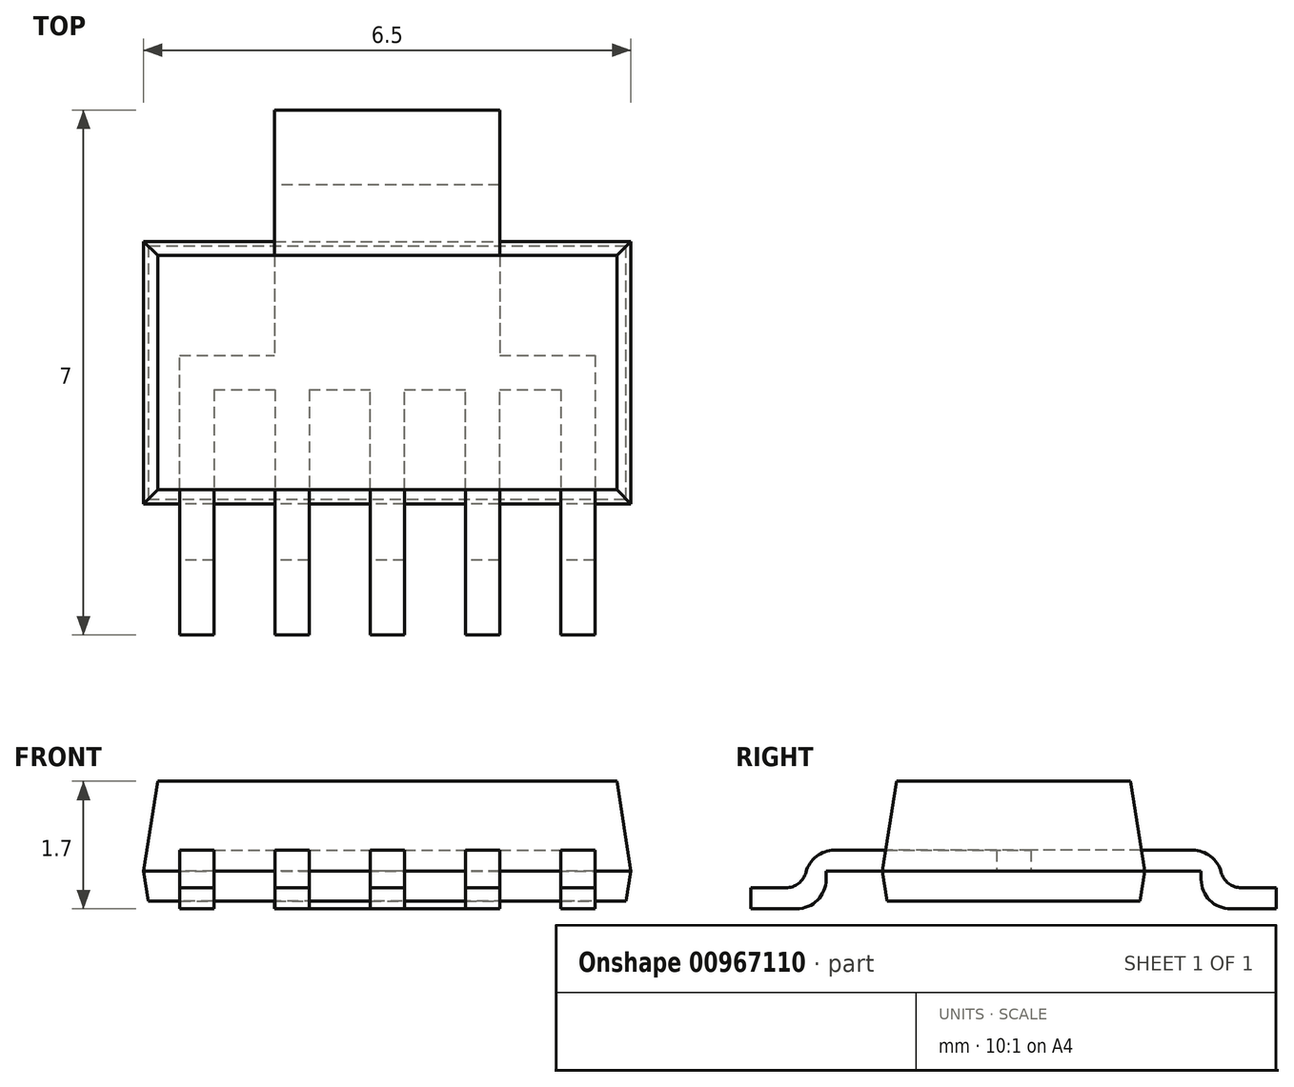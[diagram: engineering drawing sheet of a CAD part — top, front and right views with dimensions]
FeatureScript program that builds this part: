
annotation { "Feature Type Name" : "Feature", "Feature Type Description" : "" }
export const myFeature = defineFeature(function(context is Context, id is Id, definition is map)
    precondition{}
    {
        {
            assignVariable(context, id + "F0", {"name" : "A2", "anyValue" : 1.6});
        }
        {
            assignVariable(context, id + "F1", {"name" : "A1", "anyValue" : 0.1});
        }
        {
            assignVariable(context, id + "F2", {"name" : "c", "anyValue" : 0.28});
        }
        {
            var Q0;
            Q0=qCreatedBy(makeId("Top.planeOp"),FACE);
            var sketch = newSketch(context, id + "F3", { "sketchPlane" : qUnion([Q0])});
            skLineSegment(sketch, "E0.bottom", {"start": v(3.25, -1.75) * mm, "end": v(-3.25, -1.75) * mm});
            skLineSegment(sketch, "E0.top", {"start": v(3.25, 1.75) * mm, "end": v(-3.25, 1.75) * mm});
            skLineSegment(sketch, "E0.left", {"start": v(3.25, -1.75) * mm, "end": v(3.25, 1.75) * mm});
            skLineSegment(sketch, "E0.right", {"start": v(-3.25, -1.75) * mm, "end": v(-3.25, 1.75) * mm});
            skPoint(sketch, "E0.middle", {"position": v(0, 0) * mm});
            skLineSegment(sketch, "E1.bottom", {"start": v(-2.31, 0) * mm, "end": v(-2.77, 0) * mm});
            skLineSegment(sketch, "E1.top", {"start": v(-2.31, -3.5) * mm, "end": v(-2.77, -3.5) * mm});
            skLineSegment(sketch, "E1.left", {"start": v(-2.31, 0) * mm, "end": v(-2.31, -3.5) * mm});
            skLineSegment(sketch, "E1.right", {"start": v(-2.77, 0) * mm, "end": v(-2.77, -3.5) * mm});
            skPoint(sketch, "E1.middle", {"position": v(-2.54, -1.75) * mm});
            skLineSegment(sketch, "E2.bottom", {"start": v(0.23, -3.5) * mm, "end": v(-0.23, -3.5) * mm});
            skLineSegment(sketch, "E2.top", {"start": v(0.23, 0) * mm, "end": v(-0.23, 0) * mm});
            skLineSegment(sketch, "E2.left", {"start": v(0.23, -3.5) * mm, "end": v(0.23, 0) * mm});
            skLineSegment(sketch, "E2.right", {"start": v(-0.23, -3.5) * mm, "end": v(-0.23, 0) * mm});
            skPoint(sketch, "E2.middle", {"position": v(0, -1.75) * mm});
            skLineSegment(sketch, "E3.bottom", {"start": v(2.31, 0) * mm, "end": v(2.77, 0) * mm});
            skLineSegment(sketch, "E3.top", {"start": v(2.31, -3.5) * mm, "end": v(2.77, -3.5) * mm});
            skLineSegment(sketch, "E3.left", {"start": v(2.31, 0) * mm, "end": v(2.31, -3.5) * mm});
            skLineSegment(sketch, "E3.right", {"start": v(2.77, 0) * mm, "end": v(2.77, -3.5) * mm});
            skPoint(sketch, "E3.middle", {"position": v(2.54, -1.75) * mm});
            skLineSegment(sketch, "E4.bottom", {"start": v(1.5, 3.5) * mm, "end": v(-1.5, 3.5) * mm});
            skLineSegment(sketch, "E4.top", {"start": v(1.5, 0) * mm, "end": v(-1.5, 0) * mm});
            skLineSegment(sketch, "E4.left", {"start": v(1.5, 3.5) * mm, "end": v(1.5, 0) * mm});
            skLineSegment(sketch, "E4.right", {"start": v(-1.5, 3.5) * mm, "end": v(-1.5, 0) * mm});
            skPoint(sketch, "E4.middle", {"position": v(0, 1.75) * mm});
            skLineSegment(sketch, "E5", {"start": v(0, 0) * mm, "end": v(0, 1.75) * mm, "construction": true});
            skLineSegment(sketch, "E6", {"start": v(0, 0) * mm, "end": v(0, -1.75) * mm, "construction": true});
            skLineSegment(sketch, "E7.bottom", {"start": v(-2.77, -0.23) * mm, "end": v(2.77, -0.23) * mm});
            skLineSegment(sketch, "E7.top", {"start": v(-2.77, 0.23) * mm, "end": v(2.77, 0.23) * mm});
            skLineSegment(sketch, "E7.left", {"start": v(-2.77, -0.23) * mm, "end": v(-2.77, 0.23) * mm});
            skLineSegment(sketch, "E7.right", {"start": v(2.77, -0.23) * mm, "end": v(2.77, 0.23) * mm});
            skLineSegment(sketch, "E8", {"start": v(-2.77, -2.78) * mm, "end": v(2.77, -2.78) * mm});
            skLineSegment(sketch, "E9", {"start": v(2.77, -2.5) * mm, "end": v(-2.77, -2.5) * mm});
            skLineSegment(sketch, "E10", {"start": v(-1.5, 2.78) * mm, "end": v(1.5, 2.78) * mm});
            skLineSegment(sketch, "E11", {"start": v(1.5, 2.5) * mm, "end": v(-1.5, 2.5) * mm});
            skLineSegment(sketch, "E12.bottom", {"start": v(-1.04, 0) * mm, "end": v(-1.5, 0) * mm});
            skLineSegment(sketch, "E12.top", {"start": v(-1.04, -3.5) * mm, "end": v(-1.5, -3.5) * mm});
            skLineSegment(sketch, "E12.left", {"start": v(-1.04, 0) * mm, "end": v(-1.04, -3.5) * mm});
            skLineSegment(sketch, "E12.right", {"start": v(-1.5, 0) * mm, "end": v(-1.5, -3.5) * mm});
            skPoint(sketch, "E12.middle", {"position": v(-1.27, -1.75) * mm});
            skLineSegment(sketch, "E13.bottom", {"start": v(1.04, -3.5) * mm, "end": v(1.5, -3.5) * mm});
            skLineSegment(sketch, "E13.top", {"start": v(1.04, 0) * mm, "end": v(1.5, 0) * mm});
            skLineSegment(sketch, "E13.left", {"start": v(1.04, -3.5) * mm, "end": v(1.04, 0) * mm});
            skLineSegment(sketch, "E13.right", {"start": v(1.5, -3.5) * mm, "end": v(1.5, 0) * mm});
            skPoint(sketch, "E13.middle", {"position": v(1.27, -1.75) * mm});
            skLineSegment(sketch, "E14", {"start": v(1.5, -2.78) * mm, "end": v(2.77, -2.78) * mm});
            skLineSegment(sketch, "E15", {"start": v(1.5, -2.5) * mm, "end": v(2.77, -2.5) * mm});
            skLineSegment(sketch, "E16", {"start": v(-1.5, -2.5) * mm, "end": v(-2.77, -2.5) * mm});
            skLineSegment(sketch, "E17", {"start": v(-1.5, -2.78) * mm, "end": v(-2.77, -2.78) * mm});
            skLineSegment(sketch, "E18", {"start": v(0, -1.75) * mm, "end": v(-1.27, -1.75) * mm, "construction": true});
            skLineSegment(sketch, "E19", {"start": v(-1.27, -1.75) * mm, "end": v(-2.54, -1.75) * mm, "construction": true});
            skLineSegment(sketch, "E20", {"start": v(0, -1.75) * mm, "end": v(1.27, -1.75) * mm, "construction": true});
            skLineSegment(sketch, "E21", {"start": v(1.27, -1.75) * mm, "end": v(2.54, -1.75) * mm, "construction": true});
            skSolve(sketch);
        }
        {
            var Q0;
            {var subQ4=sQuery(id+"F3.wireOp",EDGE,"E0.left");Q0=makeQuery(id+"F3.imprint","IMPRINT",FACE,{"disambiguationData":[TD([[makeQuery(id+"F3.imprint","IMPRINT",EDGE,{"derivedFrom":subQ4}),1.0]])]});}
            var Q1;
            {var subQ0=sQuery(id+"F3.wireOp",EDGE,"E4.left");var subQ1=sQuery(id+"F3.wireOp",EDGE,"E0.top");var subQ2=makeQuery(id+"F3.imprint","INTERSECT",VERTEX,{"derivedFrom":[subQ1,subQ0]});Q1=makeQuery(id+"F3.imprint","IMPRINT",FACE,{"disambiguationData":[TD([[makeQuery(id+"F3.imprint","IMPRINT",EDGE,{"disambiguationData":[TD([[subQ2,-1.0]])],"derivedFrom":subQ1}),1.0]])]});}
            var Q2;
            {var subQ0=sQuery(id+"F3.wireOp",EDGE,"E3.left");var subQ1=sQuery(id+"F3.wireOp",EDGE,"E0.bottom");var subQ2=makeQuery(id+"F3.imprint","INTERSECT",VERTEX,{"derivedFrom":[subQ1,subQ0]});Q2=makeQuery(id+"F3.imprint","IMPRINT",FACE,{"disambiguationData":[TD([[makeQuery(id+"F3.imprint","IMPRINT",EDGE,{"disambiguationData":[TD([[subQ2,-1.0]])],"derivedFrom":subQ1}),-1.0]])]});}
            var Q3;
            {var subQ3=sQuery(id+"F3.wireOp",EDGE,"E2.top");Q3=makeQuery(id+"F3.imprint","IMPRINT",FACE,{"disambiguationData":[TD([[makeQuery(id+"F3.imprint","IMPRINT",EDGE,{"derivedFrom":subQ3}),-1.0]])]});}
            var Q4;
            {var subQ0=sQuery(id+"F3.wireOp",EDGE,"E3.left");var subQ1=sQuery(id+"F3.wireOp",EDGE,"E0.bottom");var subQ2=makeQuery(id+"F3.imprint","INTERSECT",VERTEX,{"derivedFrom":[subQ1,subQ0]});Q4=makeQuery(id+"F3.imprint","IMPRINT",FACE,{"disambiguationData":[TD([[makeQuery(id+"F3.imprint","IMPRINT",EDGE,{"disambiguationData":[TD([[subQ2,1.0]])],"derivedFrom":subQ1}),-1.0]])]});}
            var Q5;
            {var subQ0=sQuery(id+"F3.wireOp",EDGE,"E2.right");var subQ1=sQuery(id+"F3.wireOp",EDGE,"E0.bottom");var subQ2=makeQuery(id+"F3.imprint","INTERSECT",VERTEX,{"derivedFrom":[subQ1,subQ0]});Q5=makeQuery(id+"F3.imprint","IMPRINT",FACE,{"disambiguationData":[TD([[makeQuery(id+"F3.imprint","IMPRINT",EDGE,{"disambiguationData":[TD([[subQ2,1.0]])],"derivedFrom":subQ1}),-1.0]])]});}
            var Q6;
            {var subQ0=sQuery(id+"F3.wireOp",EDGE,"E2.top");Q6=makeQuery(id+"F3.imprint","IMPRINT",FACE,{"disambiguationData":[TD([[makeQuery(id+"F3.imprint","IMPRINT",EDGE,{"derivedFrom":subQ0}),1.0]])]});}
            var Q7;
            {var subQ0=sQuery(id+"F3.wireOp",EDGE,"E2.right");var subQ1=sQuery(id+"F3.wireOp",EDGE,"E0.bottom");var subQ2=makeQuery(id+"F3.imprint","INTERSECT",VERTEX,{"derivedFrom":[subQ1,subQ0]});Q7=makeQuery(id+"F3.imprint","IMPRINT",FACE,{"disambiguationData":[TD([[makeQuery(id+"F3.imprint","IMPRINT",EDGE,{"disambiguationData":[TD([[subQ2,-1.0]])],"derivedFrom":subQ1}),-1.0]])]});}
            var Q8;
            {var subQ4=sQuery(id+"F3.wireOp",EDGE,"E0.right");Q8=makeQuery(id+"F3.imprint","IMPRINT",FACE,{"disambiguationData":[TD([[makeQuery(id+"F3.imprint","IMPRINT",EDGE,{"derivedFrom":subQ4}),-1.0]])]});}
            var Q9;
            {var subQ0=sQuery(id+"F3.wireOp",EDGE,"E1.right");var subQ1=sQuery(id+"F3.wireOp",EDGE,"E0.bottom");var subQ2=makeQuery(id+"F3.imprint","INTERSECT",VERTEX,{"derivedFrom":[subQ1,subQ0]});Q9=makeQuery(id+"F3.imprint","IMPRINT",FACE,{"disambiguationData":[TD([[makeQuery(id+"F3.imprint","IMPRINT",EDGE,{"disambiguationData":[TD([[subQ2,1.0]])],"derivedFrom":subQ1}),-1.0]])]});}
            var Q10;
            {var subQ1=sQuery(id+"F3.wireOp",EDGE,"E2.left");var subQ3=sQuery(id+"F3.wireOp",EDGE,"E7.bottom");var subQ4=makeQuery(id+"F3.imprint","INTERSECT",VERTEX,{"derivedFrom":[subQ1,subQ3]});Q10=makeQuery(id+"F3.imprint","IMPRINT",FACE,{"disambiguationData":[TD([[makeQuery(id+"F3.imprint","IMPRINT",EDGE,{"disambiguationData":[TD([[subQ4,-1.0]])],"derivedFrom":subQ3}),1.0]])]});}
            var Q11;
            {var subQ0=sQuery(id+"F3.wireOp",EDGE,"E2.left");var subQ1=sQuery(id+"F3.wireOp",EDGE,"E0.bottom");var subQ2=makeQuery(id+"F3.imprint","INTERSECT",VERTEX,{"derivedFrom":[subQ1,subQ0]});Q11=makeQuery(id+"F3.imprint","IMPRINT",FACE,{"disambiguationData":[TD([[makeQuery(id+"F3.imprint","IMPRINT",EDGE,{"disambiguationData":[TD([[subQ2,1.0]])],"derivedFrom":subQ1}),-1.0]])]});}
            var Q12;
            {var subQ0=sQuery(id+"F3.wireOp",EDGE,"E13.left");var subQ1=sQuery(id+"F3.wireOp",EDGE,"E0.bottom");var subQ2=makeQuery(id+"F3.imprint","INTERSECT",VERTEX,{"derivedFrom":[subQ1,subQ0]});Q12=makeQuery(id+"F3.imprint","IMPRINT",FACE,{"disambiguationData":[TD([[makeQuery(id+"F3.imprint","IMPRINT",EDGE,{"disambiguationData":[TD([[subQ2,1.0]])],"derivedFrom":subQ1}),-1.0]])]});}
            var Q13;
            {var subQ10=sQuery(id+"F3.wireOp",EDGE,"E3.bottom");Q13=makeQuery(id+"F3.imprint","IMPRINT",FACE,{"disambiguationData":[TD([[makeQuery(id+"F3.imprint","IMPRINT",EDGE,{"derivedFrom":subQ10}),1.0]])]});}
            var Q14;
            {var subQ0=sQuery(id+"F3.wireOp",EDGE,"E13.right");var subQ1=sQuery(id+"F3.wireOp",EDGE,"E4.top");var subQ2=makeQuery(id+"F3.imprint","INTERSECT",VERTEX,{"derivedFrom":[subQ1,subQ0]});Q14=makeQuery(id+"F3.imprint","IMPRINT",FACE,{"disambiguationData":[TD([[makeQuery(id+"F3.imprint","IMPRINT",EDGE,{"disambiguationData":[TD([[subQ2,-1.0]])],"derivedFrom":subQ1}),1.0]])]});}
            var Q15;
            {var subQ3=sQuery(id+"F3.wireOp",EDGE,"E7.bottom");var subQ5=sQuery(id+"F3.wireOp",EDGE,"E12.left");var subQ6=makeQuery(id+"F3.imprint","INTERSECT",VERTEX,{"derivedFrom":[subQ3,subQ5]});Q15=makeQuery(id+"F3.imprint","IMPRINT",FACE,{"disambiguationData":[TD([[makeQuery(id+"F3.imprint","IMPRINT",EDGE,{"disambiguationData":[TD([[subQ6,-1.0]])],"derivedFrom":subQ3}),1.0]])]});}
            var Q16;
            {var subQ0=sQuery(id+"F3.wireOp",EDGE,"E12.left");var subQ1=sQuery(id+"F3.wireOp",EDGE,"E0.bottom");var subQ2=makeQuery(id+"F3.imprint","INTERSECT",VERTEX,{"derivedFrom":[subQ1,subQ0]});Q16=makeQuery(id+"F3.imprint","IMPRINT",FACE,{"disambiguationData":[TD([[makeQuery(id+"F3.imprint","IMPRINT",EDGE,{"disambiguationData":[TD([[subQ2,-1.0]])],"derivedFrom":subQ1}),-1.0]])]});}
            var Q17;
            {var subQ0=sQuery(id+"F3.wireOp",EDGE,"E12.left");var subQ1=sQuery(id+"F3.wireOp",EDGE,"E4.top");var subQ2=makeQuery(id+"F3.imprint","INTERSECT",VERTEX,{"derivedFrom":[subQ1,subQ0]});Q17=makeQuery(id+"F3.imprint","IMPRINT",FACE,{"disambiguationData":[TD([[makeQuery(id+"F3.imprint","IMPRINT",EDGE,{"disambiguationData":[TD([[subQ2,-1.0]])],"derivedFrom":subQ1}),1.0]])]});}
            var Q18;
            {var subQ8=sQuery(id+"F3.wireOp",EDGE,"E1.bottom");Q18=makeQuery(id+"F3.imprint","IMPRINT",FACE,{"disambiguationData":[TD([[makeQuery(id+"F3.imprint","IMPRINT",EDGE,{"derivedFrom":subQ8}),-1.0]])]});}
            var Q19;
            {var subQ0=sQuery(id+"F3.wireOp",EDGE,"E1.left");var subQ1=sQuery(id+"F3.wireOp",EDGE,"E0.bottom");var subQ2=makeQuery(id+"F3.imprint","INTERSECT",VERTEX,{"derivedFrom":[subQ1,subQ0]});Q19=makeQuery(id+"F3.imprint","IMPRINT",FACE,{"disambiguationData":[TD([[makeQuery(id+"F3.imprint","IMPRINT",EDGE,{"disambiguationData":[TD([[subQ2,1.0]])],"derivedFrom":subQ1}),-1.0]])]});}
            var Q20;
            {var subQ0=sQuery(id+"F3.wireOp",EDGE,"E1.bottom");Q20=makeQuery(id+"F3.imprint","IMPRINT",FACE,{"disambiguationData":[TD([[makeQuery(id+"F3.imprint","IMPRINT",EDGE,{"derivedFrom":subQ0}),1.0]])]});}
            var Q21;
            {var subQ0=sQuery(id+"F3.wireOp",EDGE,"E3.bottom");Q21=makeQuery(id+"F3.imprint","IMPRINT",FACE,{"disambiguationData":[TD([[makeQuery(id+"F3.imprint","IMPRINT",EDGE,{"derivedFrom":subQ0}),-1.0]])]});}
            extrude(context, id + "F4", {"entities" : qUnion([Q0, Q1, Q2, Q3, Q4, Q5, Q6, Q7, Q8, Q9, Q10, Q11, Q12, Q13, Q14, Q15, Q16, Q17, Q18, Q19, Q20, Q21]), "depth" : (getVariable(context, 'A2') - 0.4) * mm, "offsetDistance" : 25 * mm, "hasDraft" : true, "draftAngle" : 9 * degree, "draftPullDirection" : true});
        }
        {
            var Q0;
            Q0=makeQuery(id+"F4.opExtrude","CAP_FACE",FACE,{"disambiguationData":[OSD([sQuery(id+"F3.wireOp",EDGE,"E0.bottom"),sQuery(id+"F3.wireOp",EDGE,"E0.top"),sQuery(id+"F3.wireOp",EDGE,"E0.left"),sQuery(id+"F3.wireOp",EDGE,"E0.right")])],"isStart":true});
            extrude(context, id + "F5", {"entities" : qUnion([Q0]), "operationType" : NewBodyOperationType.ADD, "depth" : 0.4 * mm, "offsetDistance" : 25 * mm, "hasDraft" : true, "draftAngle" : 9 * degree, "draftPullDirection" : true});
        }
        {
            var Q0;
            {var subQ0=sQuery(id+"F3.wireOp",EDGE,"E4.left");var subQ1=sQuery(id+"F3.wireOp",EDGE,"E0.top");var subQ2=makeQuery(id+"F3.imprint","INTERSECT",VERTEX,{"derivedFrom":[subQ1,subQ0]});Q0=makeQuery(id+"F3.imprint","IMPRINT",FACE,{"disambiguationData":[TD([[makeQuery(id+"F3.imprint","IMPRINT",EDGE,{"disambiguationData":[TD([[subQ2,-1.0]])],"derivedFrom":subQ1}),1.0]])]});}
            var Q1;
            {var subQ0=sQuery(id+"F3.wireOp",EDGE,"E12.left");var subQ1=sQuery(id+"F3.wireOp",EDGE,"E0.bottom");var subQ2=makeQuery(id+"F3.imprint","INTERSECT",VERTEX,{"derivedFrom":[subQ1,subQ0]});Q1=makeQuery(id+"F3.imprint","IMPRINT",FACE,{"disambiguationData":[TD([[makeQuery(id+"F3.imprint","IMPRINT",EDGE,{"disambiguationData":[TD([[subQ2,-1.0]])],"derivedFrom":subQ1}),-1.0]])]});}
            var Q2;
            {var subQ0=sQuery(id+"F3.wireOp",EDGE,"E12.left");var subQ1=sQuery(id+"F3.wireOp",EDGE,"E0.bottom");var subQ2=makeQuery(id+"F3.imprint","INTERSECT",VERTEX,{"derivedFrom":[subQ1,subQ0]});Q2=makeQuery(id+"F3.imprint","IMPRINT",FACE,{"disambiguationData":[TD([[makeQuery(id+"F3.imprint","IMPRINT",EDGE,{"disambiguationData":[TD([[subQ2,-1.0]])],"derivedFrom":subQ1}),1.0]])]});}
            var Q3;
            {var subQ8=sQuery(id+"F3.wireOp",EDGE,"E1.bottom");Q3=makeQuery(id+"F3.imprint","IMPRINT",FACE,{"disambiguationData":[TD([[makeQuery(id+"F3.imprint","IMPRINT",EDGE,{"derivedFrom":subQ8}),-1.0]])]});}
            var Q4;
            {var subQ0=sQuery(id+"F3.wireOp",EDGE,"E12.left");var subQ1=sQuery(id+"F3.wireOp",EDGE,"E4.top");var subQ2=makeQuery(id+"F3.imprint","INTERSECT",VERTEX,{"derivedFrom":[subQ1,subQ0]});Q4=makeQuery(id+"F3.imprint","IMPRINT",FACE,{"disambiguationData":[TD([[makeQuery(id+"F3.imprint","IMPRINT",EDGE,{"disambiguationData":[TD([[subQ2,-1.0]])],"derivedFrom":subQ1}),1.0]])]});}
            var Q5;
            {var subQ3=sQuery(id+"F3.wireOp",EDGE,"E7.bottom");var subQ5=sQuery(id+"F3.wireOp",EDGE,"E12.left");var subQ6=makeQuery(id+"F3.imprint","INTERSECT",VERTEX,{"derivedFrom":[subQ3,subQ5]});Q5=makeQuery(id+"F3.imprint","IMPRINT",FACE,{"disambiguationData":[TD([[makeQuery(id+"F3.imprint","IMPRINT",EDGE,{"disambiguationData":[TD([[subQ6,-1.0]])],"derivedFrom":subQ3}),1.0]])]});}
            var Q6;
            {var subQ3=sQuery(id+"F3.wireOp",EDGE,"E2.top");Q6=makeQuery(id+"F3.imprint","IMPRINT",FACE,{"disambiguationData":[TD([[makeQuery(id+"F3.imprint","IMPRINT",EDGE,{"derivedFrom":subQ3}),-1.0]])]});}
            var Q7;
            {var subQ0=sQuery(id+"F3.wireOp",EDGE,"E1.bottom");Q7=makeQuery(id+"F3.imprint","IMPRINT",FACE,{"disambiguationData":[TD([[makeQuery(id+"F3.imprint","IMPRINT",EDGE,{"derivedFrom":subQ0}),1.0]])]});}
            var Q8;
            {var subQ0=sQuery(id+"F3.wireOp",EDGE,"E1.right");var subQ1=sQuery(id+"F3.wireOp",EDGE,"E0.bottom");var subQ2=makeQuery(id+"F3.imprint","INTERSECT",VERTEX,{"derivedFrom":[subQ1,subQ0]});Q8=makeQuery(id+"F3.imprint","IMPRINT",FACE,{"disambiguationData":[TD([[makeQuery(id+"F3.imprint","IMPRINT",EDGE,{"disambiguationData":[TD([[subQ2,1.0]])],"derivedFrom":subQ1}),-1.0]])]});}
            var Q9;
            {var subQ0=sQuery(id+"F3.wireOp",EDGE,"E1.right");var subQ1=sQuery(id+"F3.wireOp",EDGE,"E0.bottom");var subQ2=makeQuery(id+"F3.imprint","INTERSECT",VERTEX,{"derivedFrom":[subQ1,subQ0]});Q9=makeQuery(id+"F3.imprint","IMPRINT",FACE,{"disambiguationData":[TD([[makeQuery(id+"F3.imprint","IMPRINT",EDGE,{"disambiguationData":[TD([[subQ2,1.0]])],"derivedFrom":subQ1}),1.0]])]});}
            var Q10;
            {var subQ0=sQuery(id+"F3.wireOp",EDGE,"E8");var subQ1=sQuery(id+"F3.wireOp",EDGE,"E1.left");var subQ2=makeQuery(id+"F3.imprint","INTERSECT",VERTEX,{"derivedFrom":[subQ1,subQ0]});Q10=makeQuery(id+"F3.imprint","IMPRINT",FACE,{"disambiguationData":[TD([[makeQuery(id+"F3.imprint","IMPRINT",EDGE,{"disambiguationData":[TD([[subQ2,1.0]])],"derivedFrom":subQ1}),-1.0]])]});}
            var Q11;
            {var subQ0=sQuery(id+"F3.wireOp",EDGE,"E12.left");var subQ1=sQuery(id+"F3.wireOp",EDGE,"E8");var subQ2=makeQuery(id+"F3.imprint","INTERSECT",VERTEX,{"derivedFrom":[subQ1,subQ0]});Q11=makeQuery(id+"F3.imprint","IMPRINT",FACE,{"disambiguationData":[TD([[makeQuery(id+"F3.imprint","IMPRINT",EDGE,{"disambiguationData":[TD([[subQ2,1.0]])],"derivedFrom":subQ1}),1.0]])]});}
            var Q12;
            {var subQ0=sQuery(id+"F3.wireOp",EDGE,"E2.right");var subQ1=sQuery(id+"F3.wireOp",EDGE,"E0.bottom");var subQ2=makeQuery(id+"F3.imprint","INTERSECT",VERTEX,{"derivedFrom":[subQ1,subQ0]});Q12=makeQuery(id+"F3.imprint","IMPRINT",FACE,{"disambiguationData":[TD([[makeQuery(id+"F3.imprint","IMPRINT",EDGE,{"disambiguationData":[TD([[subQ2,1.0]])],"derivedFrom":subQ1}),1.0]])]});}
            var Q13;
            {var subQ0=sQuery(id+"F3.wireOp",EDGE,"E2.right");var subQ1=sQuery(id+"F3.wireOp",EDGE,"E0.bottom");var subQ2=makeQuery(id+"F3.imprint","INTERSECT",VERTEX,{"derivedFrom":[subQ1,subQ0]});Q13=makeQuery(id+"F3.imprint","IMPRINT",FACE,{"disambiguationData":[TD([[makeQuery(id+"F3.imprint","IMPRINT",EDGE,{"disambiguationData":[TD([[subQ2,1.0]])],"derivedFrom":subQ1}),-1.0]])]});}
            var Q14;
            {var subQ0=sQuery(id+"F3.wireOp",EDGE,"E8");var subQ1=sQuery(id+"F3.wireOp",EDGE,"E2.left");var subQ2=makeQuery(id+"F3.imprint","INTERSECT",VERTEX,{"derivedFrom":[subQ1,subQ0]});Q14=makeQuery(id+"F3.imprint","IMPRINT",FACE,{"disambiguationData":[TD([[makeQuery(id+"F3.imprint","IMPRINT",EDGE,{"disambiguationData":[TD([[subQ2,-1.0]])],"derivedFrom":subQ1}),1.0]])]});}
            var Q15;
            {var subQ0=sQuery(id+"F3.wireOp",EDGE,"E13.left");var subQ1=sQuery(id+"F3.wireOp",EDGE,"E0.bottom");var subQ2=makeQuery(id+"F3.imprint","INTERSECT",VERTEX,{"derivedFrom":[subQ1,subQ0]});Q15=makeQuery(id+"F3.imprint","IMPRINT",FACE,{"disambiguationData":[TD([[makeQuery(id+"F3.imprint","IMPRINT",EDGE,{"disambiguationData":[TD([[subQ2,1.0]])],"derivedFrom":subQ1}),1.0]])]});}
            var Q16;
            {var subQ0=sQuery(id+"F3.wireOp",EDGE,"E13.left");var subQ1=sQuery(id+"F3.wireOp",EDGE,"E0.bottom");var subQ2=makeQuery(id+"F3.imprint","INTERSECT",VERTEX,{"derivedFrom":[subQ1,subQ0]});Q16=makeQuery(id+"F3.imprint","IMPRINT",FACE,{"disambiguationData":[TD([[makeQuery(id+"F3.imprint","IMPRINT",EDGE,{"disambiguationData":[TD([[subQ2,1.0]])],"derivedFrom":subQ1}),-1.0]])]});}
            var Q17;
            {var subQ0=sQuery(id+"F3.wireOp",EDGE,"E13.left");var subQ1=sQuery(id+"F3.wireOp",EDGE,"E8");var subQ2=makeQuery(id+"F3.imprint","INTERSECT",VERTEX,{"derivedFrom":[subQ1,subQ0]});Q17=makeQuery(id+"F3.imprint","IMPRINT",FACE,{"disambiguationData":[TD([[makeQuery(id+"F3.imprint","IMPRINT",EDGE,{"disambiguationData":[TD([[subQ2,-1.0]])],"derivedFrom":subQ1}),1.0]])]});}
            var Q18;
            {var subQ0=sQuery(id+"F3.wireOp",EDGE,"E3.left");var subQ1=sQuery(id+"F3.wireOp",EDGE,"E0.bottom");var subQ2=makeQuery(id+"F3.imprint","INTERSECT",VERTEX,{"derivedFrom":[subQ1,subQ0]});Q18=makeQuery(id+"F3.imprint","IMPRINT",FACE,{"disambiguationData":[TD([[makeQuery(id+"F3.imprint","IMPRINT",EDGE,{"disambiguationData":[TD([[subQ2,1.0]])],"derivedFrom":subQ1}),1.0]])]});}
            var Q19;
            {var subQ0=sQuery(id+"F3.wireOp",EDGE,"E8");var subQ1=sQuery(id+"F3.wireOp",EDGE,"E3.left");var subQ2=makeQuery(id+"F3.imprint","INTERSECT",VERTEX,{"derivedFrom":[subQ1,subQ0]});Q19=makeQuery(id+"F3.imprint","IMPRINT",FACE,{"disambiguationData":[TD([[makeQuery(id+"F3.imprint","IMPRINT",EDGE,{"disambiguationData":[TD([[subQ2,1.0]])],"derivedFrom":subQ1}),1.0]])]});}
            var Q20;
            {var subQ0=sQuery(id+"F3.wireOp",EDGE,"E3.left");var subQ1=sQuery(id+"F3.wireOp",EDGE,"E0.bottom");var subQ2=makeQuery(id+"F3.imprint","INTERSECT",VERTEX,{"derivedFrom":[subQ1,subQ0]});Q20=makeQuery(id+"F3.imprint","IMPRINT",FACE,{"disambiguationData":[TD([[makeQuery(id+"F3.imprint","IMPRINT",EDGE,{"disambiguationData":[TD([[subQ2,1.0]])],"derivedFrom":subQ1}),-1.0]])]});}
            var Q21;
            {var subQ0=sQuery(id+"F3.wireOp",EDGE,"E3.bottom");Q21=makeQuery(id+"F3.imprint","IMPRINT",FACE,{"disambiguationData":[TD([[makeQuery(id+"F3.imprint","IMPRINT",EDGE,{"derivedFrom":subQ0}),-1.0]])]});}
            var Q22;
            {var subQ10=sQuery(id+"F3.wireOp",EDGE,"E3.bottom");Q22=makeQuery(id+"F3.imprint","IMPRINT",FACE,{"disambiguationData":[TD([[makeQuery(id+"F3.imprint","IMPRINT",EDGE,{"derivedFrom":subQ10}),1.0]])]});}
            var Q23;
            {var subQ0=sQuery(id+"F3.wireOp",EDGE,"E13.right");var subQ1=sQuery(id+"F3.wireOp",EDGE,"E4.top");var subQ2=makeQuery(id+"F3.imprint","INTERSECT",VERTEX,{"derivedFrom":[subQ1,subQ0]});Q23=makeQuery(id+"F3.imprint","IMPRINT",FACE,{"disambiguationData":[TD([[makeQuery(id+"F3.imprint","IMPRINT",EDGE,{"disambiguationData":[TD([[subQ2,-1.0]])],"derivedFrom":subQ1}),1.0]])]});}
            var Q24;
            {var subQ0=sQuery(id+"F3.wireOp",EDGE,"E2.top");Q24=makeQuery(id+"F3.imprint","IMPRINT",FACE,{"disambiguationData":[TD([[makeQuery(id+"F3.imprint","IMPRINT",EDGE,{"derivedFrom":subQ0}),1.0]])]});}
            var Q25;
            {var subQ1=sQuery(id+"F3.wireOp",EDGE,"E2.left");var subQ3=sQuery(id+"F3.wireOp",EDGE,"E7.bottom");var subQ4=makeQuery(id+"F3.imprint","INTERSECT",VERTEX,{"derivedFrom":[subQ1,subQ3]});Q25=makeQuery(id+"F3.imprint","IMPRINT",FACE,{"disambiguationData":[TD([[makeQuery(id+"F3.imprint","IMPRINT",EDGE,{"disambiguationData":[TD([[subQ4,-1.0]])],"derivedFrom":subQ3}),1.0]])]});}
            var Q26;
            {var subQ5=sQuery(id+"F3.wireOp",EDGE,"E11");Q26=makeQuery(id+"F3.imprint","IMPRINT",FACE,{"disambiguationData":[TD([[makeQuery(id+"F3.imprint","IMPRINT",EDGE,{"derivedFrom":subQ5}),1.0]])]});}
            var Q27;
            {var subQ0=sQuery(id+"F3.wireOp",EDGE,"E10");Q27=makeQuery(id+"F3.imprint","IMPRINT",FACE,{"disambiguationData":[TD([[makeQuery(id+"F3.imprint","IMPRINT",EDGE,{"derivedFrom":subQ0}),-1.0]])]});}
            extrude(context, id + "F6", {"entities" : qUnion([Q0, Q1, Q2, Q3, Q4, Q5, Q6, Q7, Q8, Q9, Q10, Q11, Q12, Q13, Q14, Q15, Q16, Q17, Q18, Q19, Q20, Q21, Q22, Q23, Q24, Q25, Q26, Q27]), "depth" : getVariable(context, 'c') * mm, "offsetDistance" : 25 * mm});
        }
        {
            var Q0;
            {var subQ0=sQuery(id+"F3.wireOp",EDGE,"E8");var subQ1=sQuery(id+"F3.wireOp",EDGE,"E3.left");var subQ2=makeQuery(id+"F3.imprint","INTERSECT",VERTEX,{"derivedFrom":[subQ1,subQ0]});Q0=makeQuery(id+"F3.imprint","IMPRINT",FACE,{"disambiguationData":[TD([[makeQuery(id+"F3.imprint","IMPRINT",EDGE,{"disambiguationData":[TD([[subQ2,1.0]])],"derivedFrom":subQ1}),1.0]])]});}
            var Q1;
            {var subQ0=sQuery(id+"F3.wireOp",EDGE,"E3.top");Q1=makeQuery(id+"F3.imprint","IMPRINT",FACE,{"disambiguationData":[TD([[makeQuery(id+"F3.imprint","IMPRINT",EDGE,{"derivedFrom":subQ0}),1.0]])]});}
            var Q2;
            {var subQ0=sQuery(id+"F3.wireOp",EDGE,"E13.left");var subQ1=sQuery(id+"F3.wireOp",EDGE,"E8");var subQ2=makeQuery(id+"F3.imprint","INTERSECT",VERTEX,{"derivedFrom":[subQ1,subQ0]});Q2=makeQuery(id+"F3.imprint","IMPRINT",FACE,{"disambiguationData":[TD([[makeQuery(id+"F3.imprint","IMPRINT",EDGE,{"disambiguationData":[TD([[subQ2,-1.0]])],"derivedFrom":subQ1}),1.0]])]});}
            var Q3;
            {var subQ5=sQuery(id+"F3.wireOp",EDGE,"E13.bottom");Q3=makeQuery(id+"F3.imprint","IMPRINT",FACE,{"disambiguationData":[TD([[makeQuery(id+"F3.imprint","IMPRINT",EDGE,{"derivedFrom":subQ5}),1.0]])]});}
            var Q4;
            {var subQ0=sQuery(id+"F3.wireOp",EDGE,"E2.bottom");Q4=makeQuery(id+"F3.imprint","IMPRINT",FACE,{"disambiguationData":[TD([[makeQuery(id+"F3.imprint","IMPRINT",EDGE,{"derivedFrom":subQ0}),-1.0]])]});}
            var Q5;
            {var subQ0=sQuery(id+"F3.wireOp",EDGE,"E8");var subQ1=sQuery(id+"F3.wireOp",EDGE,"E2.left");var subQ2=makeQuery(id+"F3.imprint","INTERSECT",VERTEX,{"derivedFrom":[subQ1,subQ0]});Q5=makeQuery(id+"F3.imprint","IMPRINT",FACE,{"disambiguationData":[TD([[makeQuery(id+"F3.imprint","IMPRINT",EDGE,{"disambiguationData":[TD([[subQ2,-1.0]])],"derivedFrom":subQ1}),1.0]])]});}
            var Q6;
            {var subQ0=sQuery(id+"F3.wireOp",EDGE,"E12.left");var subQ1=sQuery(id+"F3.wireOp",EDGE,"E8");var subQ2=makeQuery(id+"F3.imprint","INTERSECT",VERTEX,{"derivedFrom":[subQ1,subQ0]});Q6=makeQuery(id+"F3.imprint","IMPRINT",FACE,{"disambiguationData":[TD([[makeQuery(id+"F3.imprint","IMPRINT",EDGE,{"disambiguationData":[TD([[subQ2,1.0]])],"derivedFrom":subQ1}),1.0]])]});}
            var Q7;
            {var subQ5=sQuery(id+"F3.wireOp",EDGE,"E12.top");Q7=makeQuery(id+"F3.imprint","IMPRINT",FACE,{"disambiguationData":[TD([[makeQuery(id+"F3.imprint","IMPRINT",EDGE,{"derivedFrom":subQ5}),-1.0]])]});}
            var Q8;
            {var subQ0=sQuery(id+"F3.wireOp",EDGE,"E8");var subQ1=sQuery(id+"F3.wireOp",EDGE,"E1.left");var subQ2=makeQuery(id+"F3.imprint","INTERSECT",VERTEX,{"derivedFrom":[subQ1,subQ0]});Q8=makeQuery(id+"F3.imprint","IMPRINT",FACE,{"disambiguationData":[TD([[makeQuery(id+"F3.imprint","IMPRINT",EDGE,{"disambiguationData":[TD([[subQ2,1.0]])],"derivedFrom":subQ1}),-1.0]])]});}
            var Q9;
            {var subQ0=sQuery(id+"F3.wireOp",EDGE,"E1.top");Q9=makeQuery(id+"F3.imprint","IMPRINT",FACE,{"disambiguationData":[TD([[makeQuery(id+"F3.imprint","IMPRINT",EDGE,{"derivedFrom":subQ0}),-1.0]])]});}
            var Q10;
            {var subQ0=sQuery(id+"F3.wireOp",EDGE,"E4.bottom");Q10=makeQuery(id+"F3.imprint","IMPRINT",FACE,{"disambiguationData":[TD([[makeQuery(id+"F3.imprint","IMPRINT",EDGE,{"derivedFrom":subQ0}),1.0]])]});}
            var Q11;
            {var subQ0=sQuery(id+"F3.wireOp",EDGE,"E10");Q11=makeQuery(id+"F3.imprint","IMPRINT",FACE,{"disambiguationData":[TD([[makeQuery(id+"F3.imprint","IMPRINT",EDGE,{"derivedFrom":subQ0}),-1.0]])]});}
            extrude(context, id + "F7", {"entities" : qUnion([Q0, Q1, Q2, Q3, Q4, Q5, Q6, Q7, Q8, Q9, Q10, Q11]), "operationType" : NewBodyOperationType.ADD, "oppositeDirection" : true, "depth" : (.4 + getVariable(context, 'A1')) * mm, "offsetDistance" : 25 * mm});
        }
        {
            var Q0;
            {var subQ0=sQuery(id+"F3.wireOp",EDGE,"E4.bottom");Q0=makeQuery(id+"F3.imprint","IMPRINT",FACE,{"disambiguationData":[TD([[makeQuery(id+"F3.imprint","IMPRINT",EDGE,{"derivedFrom":subQ0}),1.0]])]});}
            var Q1;
            {var subQ0=sQuery(id+"F3.wireOp",EDGE,"E1.top");Q1=makeQuery(id+"F3.imprint","IMPRINT",FACE,{"disambiguationData":[TD([[makeQuery(id+"F3.imprint","IMPRINT",EDGE,{"derivedFrom":subQ0}),-1.0]])]});}
            var Q2;
            {var subQ0=sQuery(id+"F3.wireOp",EDGE,"E2.bottom");Q2=makeQuery(id+"F3.imprint","IMPRINT",FACE,{"disambiguationData":[TD([[makeQuery(id+"F3.imprint","IMPRINT",EDGE,{"derivedFrom":subQ0}),-1.0]])]});}
            var Q3;
            {var subQ0=sQuery(id+"F3.wireOp",EDGE,"E3.top");Q3=makeQuery(id+"F3.imprint","IMPRINT",FACE,{"disambiguationData":[TD([[makeQuery(id+"F3.imprint","IMPRINT",EDGE,{"derivedFrom":subQ0}),1.0]])]});}
            var Q4;
            {var subQ5=sQuery(id+"F3.wireOp",EDGE,"E12.top");Q4=makeQuery(id+"F3.imprint","IMPRINT",FACE,{"disambiguationData":[TD([[makeQuery(id+"F3.imprint","IMPRINT",EDGE,{"derivedFrom":subQ5}),-1.0]])]});}
            var Q5;
            {var subQ5=sQuery(id+"F3.wireOp",EDGE,"E13.bottom");Q5=makeQuery(id+"F3.imprint","IMPRINT",FACE,{"disambiguationData":[TD([[makeQuery(id+"F3.imprint","IMPRINT",EDGE,{"derivedFrom":subQ5}),1.0]])]});}
            extrude(context, id + "F8", {"entities" : qUnion([Q0, Q1, Q2, Q3, Q4, Q5]), "operationType" : NewBodyOperationType.REMOVE, "oppositeDirection" : true, "depth" : ((0.4 + getVariable(context, 'A1')) - getVariable(context, 'c')) * mm, "offsetDistance" : 25 * mm});
        }
        {
            var Q0;
            Q0=makeQuery(id+"F6.opExtrude","CAP_EDGE",EDGE,{"disambiguationData":[OSD([sQuery(id+"F3.wireOp",EDGE,"E10")])],"isStart":false});
            var Q1;
            Q1=makeQuery(id+"F7.opExtrude","CAP_EDGE",EDGE,{"disambiguationData":[OSD([sQuery(id+"F3.wireOp",EDGE,"E11")])],"isStart":false});
            var Q2;
            {var subQ0=sQuery(id+"F3.wireOp",EDGE,"E8");Q2=makeQuery(id+"F6.opExtrude","CAP_EDGE",EDGE,{"disambiguationData":[OSD([subQ0]),TDD([makeQuery(id+"F3.imprint","IMPRINT",EDGE,{"disambiguationData":[TD([[makeQuery(id+"F3.imprint","INTERSECT",VERTEX,{"derivedFrom":[sQuery(id+"F3.wireOp",EDGE,"E1.left"),subQ0]}),1.0]])],"derivedFrom":subQ0})])],"isStart":false});}
            var Q3;
            {var subQ0=sQuery(id+"F3.wireOp",EDGE,"E8");Q3=makeQuery(id+"F6.opExtrude","CAP_EDGE",EDGE,{"disambiguationData":[OSD([subQ0]),TDD([makeQuery(id+"F3.imprint","IMPRINT",EDGE,{"disambiguationData":[TD([[makeQuery(id+"F3.imprint","INTERSECT",VERTEX,{"derivedFrom":[subQ0,sQuery(id+"F3.wireOp",EDGE,"E12.left")]}),1.0]])],"derivedFrom":subQ0})])],"isStart":false});}
            var Q4;
            {var subQ0=sQuery(id+"F3.wireOp",EDGE,"E8");Q4=makeQuery(id+"F6.opExtrude","CAP_EDGE",EDGE,{"disambiguationData":[OSD([subQ0]),TDD([makeQuery(id+"F3.imprint","IMPRINT",EDGE,{"disambiguationData":[TD([[makeQuery(id+"F3.imprint","INTERSECT",VERTEX,{"derivedFrom":[sQuery(id+"F3.wireOp",EDGE,"E2.left"),subQ0]}),1.0]])],"derivedFrom":subQ0})])],"isStart":false});}
            var Q5;
            {var subQ0=sQuery(id+"F3.wireOp",EDGE,"E8");Q5=makeQuery(id+"F6.opExtrude","CAP_EDGE",EDGE,{"disambiguationData":[OSD([subQ0]),TDD([makeQuery(id+"F3.imprint","IMPRINT",EDGE,{"disambiguationData":[TD([[makeQuery(id+"F3.imprint","INTERSECT",VERTEX,{"derivedFrom":[subQ0,sQuery(id+"F3.wireOp",EDGE,"E13.left")]}),-1.0]])],"derivedFrom":subQ0})])],"isStart":false});}
            var Q6;
            {var subQ0=sQuery(id+"F3.wireOp",EDGE,"E8");Q6=makeQuery(id+"F6.opExtrude","CAP_EDGE",EDGE,{"disambiguationData":[OSD([subQ0]),TDD([makeQuery(id+"F3.imprint","IMPRINT",EDGE,{"disambiguationData":[TD([[makeQuery(id+"F3.imprint","INTERSECT",VERTEX,{"derivedFrom":[sQuery(id+"F3.wireOp",EDGE,"E3.right"),subQ0]}),1.0]])],"derivedFrom":subQ0})])],"isStart":false});}
            var Q7;
            {var subQ0=sQuery(id+"F3.wireOp",EDGE,"E9");Q7=makeQuery(id+"F7.opExtrude","CAP_EDGE",EDGE,{"disambiguationData":[OSD([subQ0]),TDD([makeQuery(id+"F3.imprint","IMPRINT",EDGE,{"disambiguationData":[TD([[makeQuery(id+"F3.imprint","INTERSECT",VERTEX,{"derivedFrom":[subQ0,sQuery(id+"F3.wireOp",EDGE,"E12.left")]}),-1.0]])],"derivedFrom":subQ0})])],"isStart":false});}
            var Q8;
            {var subQ0=sQuery(id+"F3.wireOp",EDGE,"E9");Q8=makeQuery(id+"F7.opExtrude","CAP_EDGE",EDGE,{"disambiguationData":[OSD([subQ0]),TDD([makeQuery(id+"F3.imprint","IMPRINT",EDGE,{"disambiguationData":[TD([[makeQuery(id+"F3.imprint","INTERSECT",VERTEX,{"derivedFrom":[sQuery(id+"F3.wireOp",EDGE,"E1.right"),subQ0]}),1.0]])],"derivedFrom":subQ0})])],"isStart":false});}
            var Q9;
            {var subQ0=sQuery(id+"F3.wireOp",EDGE,"E9");Q9=makeQuery(id+"F7.opExtrude","CAP_EDGE",EDGE,{"disambiguationData":[OSD([subQ0]),TDD([makeQuery(id+"F3.imprint","IMPRINT",EDGE,{"disambiguationData":[TD([[makeQuery(id+"F3.imprint","INTERSECT",VERTEX,{"derivedFrom":[sQuery(id+"F3.wireOp",EDGE,"E2.right"),subQ0]}),1.0]])],"derivedFrom":subQ0})])],"isStart":false});}
            var Q10;
            {var subQ0=sQuery(id+"F3.wireOp",EDGE,"E9");Q10=makeQuery(id+"F7.opExtrude","CAP_EDGE",EDGE,{"disambiguationData":[OSD([subQ0]),TDD([makeQuery(id+"F3.imprint","IMPRINT",EDGE,{"disambiguationData":[TD([[makeQuery(id+"F3.imprint","INTERSECT",VERTEX,{"derivedFrom":[subQ0,sQuery(id+"F3.wireOp",EDGE,"E13.left")]}),1.0]])],"derivedFrom":subQ0})])],"isStart":false});}
            var Q11;
            {var subQ0=sQuery(id+"F3.wireOp",EDGE,"E9");Q11=makeQuery(id+"F7.opExtrude","CAP_EDGE",EDGE,{"disambiguationData":[OSD([subQ0]),TDD([makeQuery(id+"F3.imprint","IMPRINT",EDGE,{"disambiguationData":[TD([[makeQuery(id+"F3.imprint","INTERSECT",VERTEX,{"derivedFrom":[sQuery(id+"F3.wireOp",EDGE,"E3.right"),subQ0]}),-1.0]])],"derivedFrom":subQ0})])],"isStart":false});}
            fillet(context, id + "F9", {"entities" : qUnion([Q0, Q1, Q2, Q3, Q4, Q5, Q6, Q7, Q8, Q9, Q10, Q11]), "radius" : getVariable(context, 'c') * 1.4 * mm, "tangentPropagation" : true, "allowEdgeOverflow" : false});
        }
        {
            var Q0;
            Q0=makeQuery(id+"F8.boolean.opBoolean","COPY",EDGE,{"derivedFrom":makeQuery(id+"F8.opExtrude","CAP_EDGE",EDGE,{"disambiguationData":[OSD([sQuery(id+"F3.wireOp",EDGE,"E10")])],"isStart":false})});
            var Q1;
            Q1=makeQuery(id+"F7.opExtrude","CAP_EDGE",EDGE,{"disambiguationData":[OSD([sQuery(id+"F3.wireOp",EDGE,"E11")])],"isStart":true});
            var Q2;
            {var subQ0=sQuery(id+"F3.wireOp",EDGE,"E9");Q2=makeQuery(id+"F7.opExtrude","CAP_EDGE",EDGE,{"disambiguationData":[OSD([subQ0]),TDD([makeQuery(id+"F3.imprint","IMPRINT",EDGE,{"disambiguationData":[TD([[makeQuery(id+"F3.imprint","INTERSECT",VERTEX,{"derivedFrom":[sQuery(id+"F3.wireOp",EDGE,"E3.right"),subQ0]}),-1.0]])],"derivedFrom":subQ0})])],"isStart":true});}
            var Q3;
            {var subQ0=sQuery(id+"F3.wireOp",EDGE,"E9");Q3=makeQuery(id+"F7.opExtrude","CAP_EDGE",EDGE,{"disambiguationData":[OSD([subQ0]),TDD([makeQuery(id+"F3.imprint","IMPRINT",EDGE,{"disambiguationData":[TD([[makeQuery(id+"F3.imprint","INTERSECT",VERTEX,{"derivedFrom":[subQ0,sQuery(id+"F3.wireOp",EDGE,"E13.left")]}),1.0]])],"derivedFrom":subQ0})])],"isStart":true});}
            var Q4;
            {var subQ0=sQuery(id+"F3.wireOp",EDGE,"E9");Q4=makeQuery(id+"F7.opExtrude","CAP_EDGE",EDGE,{"disambiguationData":[OSD([subQ0]),TDD([makeQuery(id+"F3.imprint","IMPRINT",EDGE,{"disambiguationData":[TD([[makeQuery(id+"F3.imprint","INTERSECT",VERTEX,{"derivedFrom":[sQuery(id+"F3.wireOp",EDGE,"E2.right"),subQ0]}),1.0]])],"derivedFrom":subQ0})])],"isStart":true});}
            var Q5;
            {var subQ0=sQuery(id+"F3.wireOp",EDGE,"E9");Q5=makeQuery(id+"F7.opExtrude","CAP_EDGE",EDGE,{"disambiguationData":[OSD([subQ0]),TDD([makeQuery(id+"F3.imprint","IMPRINT",EDGE,{"disambiguationData":[TD([[makeQuery(id+"F3.imprint","INTERSECT",VERTEX,{"derivedFrom":[subQ0,sQuery(id+"F3.wireOp",EDGE,"E12.left")]}),-1.0]])],"derivedFrom":subQ0})])],"isStart":true});}
            var Q6;
            {var subQ0=sQuery(id+"F3.wireOp",EDGE,"E9");Q6=makeQuery(id+"F7.opExtrude","CAP_EDGE",EDGE,{"disambiguationData":[OSD([subQ0]),TDD([makeQuery(id+"F3.imprint","IMPRINT",EDGE,{"disambiguationData":[TD([[makeQuery(id+"F3.imprint","INTERSECT",VERTEX,{"derivedFrom":[sQuery(id+"F3.wireOp",EDGE,"E1.right"),subQ0]}),1.0]])],"derivedFrom":subQ0})])],"isStart":true});}
            var Q7;
            {var subQ0=sQuery(id+"F3.wireOp",EDGE,"E8");Q7=makeQuery(id+"F8.boolean.opBoolean","COPY",EDGE,{"derivedFrom":makeQuery(id+"F8.opExtrude","CAP_EDGE",EDGE,{"disambiguationData":[OSD([subQ0]),TDD([makeQuery(id+"F3.imprint","IMPRINT",EDGE,{"disambiguationData":[TD([[makeQuery(id+"F3.imprint","INTERSECT",VERTEX,{"derivedFrom":[sQuery(id+"F3.wireOp",EDGE,"E1.left"),subQ0]}),1.0]])],"derivedFrom":subQ0})])],"isStart":false})});}
            var Q8;
            {var subQ0=sQuery(id+"F3.wireOp",EDGE,"E8");Q8=makeQuery(id+"F8.boolean.opBoolean","COPY",EDGE,{"derivedFrom":makeQuery(id+"F8.opExtrude","CAP_EDGE",EDGE,{"disambiguationData":[OSD([subQ0]),TDD([makeQuery(id+"F3.imprint","IMPRINT",EDGE,{"disambiguationData":[TD([[makeQuery(id+"F3.imprint","INTERSECT",VERTEX,{"derivedFrom":[subQ0,sQuery(id+"F3.wireOp",EDGE,"E12.left")]}),1.0]])],"derivedFrom":subQ0})])],"isStart":false})});}
            var Q9;
            {var subQ0=sQuery(id+"F3.wireOp",EDGE,"E8");Q9=makeQuery(id+"F8.boolean.opBoolean","COPY",EDGE,{"derivedFrom":makeQuery(id+"F8.opExtrude","CAP_EDGE",EDGE,{"disambiguationData":[OSD([subQ0]),TDD([makeQuery(id+"F3.imprint","IMPRINT",EDGE,{"disambiguationData":[TD([[makeQuery(id+"F3.imprint","INTERSECT",VERTEX,{"derivedFrom":[sQuery(id+"F3.wireOp",EDGE,"E2.left"),subQ0]}),1.0]])],"derivedFrom":subQ0})])],"isStart":false})});}
            var Q10;
            {var subQ0=sQuery(id+"F3.wireOp",EDGE,"E8");Q10=makeQuery(id+"F8.boolean.opBoolean","COPY",EDGE,{"derivedFrom":makeQuery(id+"F8.opExtrude","CAP_EDGE",EDGE,{"disambiguationData":[OSD([subQ0]),TDD([makeQuery(id+"F3.imprint","IMPRINT",EDGE,{"disambiguationData":[TD([[makeQuery(id+"F3.imprint","INTERSECT",VERTEX,{"derivedFrom":[subQ0,sQuery(id+"F3.wireOp",EDGE,"E13.left")]}),-1.0]])],"derivedFrom":subQ0})])],"isStart":false})});}
            var Q11;
            {var subQ0=sQuery(id+"F3.wireOp",EDGE,"E8");Q11=makeQuery(id+"F8.boolean.opBoolean","COPY",EDGE,{"derivedFrom":makeQuery(id+"F8.opExtrude","CAP_EDGE",EDGE,{"disambiguationData":[OSD([subQ0]),TDD([makeQuery(id+"F3.imprint","IMPRINT",EDGE,{"disambiguationData":[TD([[makeQuery(id+"F3.imprint","INTERSECT",VERTEX,{"derivedFrom":[sQuery(id+"F3.wireOp",EDGE,"E3.right"),subQ0]}),1.0]])],"derivedFrom":subQ0})])],"isStart":false})});}
            fillet(context, id + "F10", {"entities" : qUnion([Q0, Q1, Q2, Q3, Q4, Q5, Q6, Q7, Q8, Q9, Q10, Q11]), "radius" : getVariable(context, 'c') * mm, "tangentPropagation" : true, "allowEdgeOverflow" : false});
        }
        {
            var Q0;
            Q0=makeQuery(id+"F7.opExtrude","CAP_FACE",FACE,{"disambiguationData":[OSD([sQuery(id+"F3.wireOp",EDGE,"E1.top"),sQuery(id+"F3.wireOp",EDGE,"E1.left"),sQuery(id+"F3.wireOp",EDGE,"E1.right"),sQuery(id+"F3.wireOp",EDGE,"E9")])],"isStart":false});
            var sketch = newSketch(context, id + "F11", { "sketchPlane" : qUnion([Q0])});
            skLineSegment(sketch, "E22.bottom", {"start": v(-2.22, 2) * mm, "end": v(-2.87, 2) * mm});
            skLineSegment(sketch, "E22.top", {"start": v(-2.22, 4) * mm, "end": v(-2.87, 4) * mm});
            skLineSegment(sketch, "E22.left", {"start": v(-2.22, 2) * mm, "end": v(-2.22, 4) * mm});
            skLineSegment(sketch, "E22.right", {"start": v(-2.87, 2) * mm, "end": v(-2.87, 4) * mm});
            skPoint(sketch, "E22.middle", {"position": v(-2.54, 3) * mm});
            skLineSegment(sketch, "E23.bottom", {"start": v(0.33, 4) * mm, "end": v(-0.33, 4) * mm});
            skLineSegment(sketch, "E23.top", {"start": v(0.33, 2) * mm, "end": v(-0.32, 2) * mm});
            skLineSegment(sketch, "E23.left", {"start": v(0.32, 4) * mm, "end": v(0.33, 2) * mm});
            skLineSegment(sketch, "E23.right", {"start": v(-0.33, 4) * mm, "end": v(-0.32, 2) * mm});
            skPoint(sketch, "E23.middle", {"position": v(0, 3) * mm});
            skLineSegment(sketch, "E24.bottom", {"start": v(2.87, 2) * mm, "end": v(2.22, 2) * mm});
            skLineSegment(sketch, "E24.top", {"start": v(2.87, 4) * mm, "end": v(2.22, 4) * mm});
            skLineSegment(sketch, "E24.left", {"start": v(2.87, 2) * mm, "end": v(2.87, 4) * mm});
            skLineSegment(sketch, "E24.right", {"start": v(2.22, 2) * mm, "end": v(2.22, 4) * mm});
            skPoint(sketch, "E24.middle", {"position": v(2.54, 3) * mm});
            skLineSegment(sketch, "E25.bottom", {"start": v(3.25, -1.75) * mm, "end": v(-3.25, -1.75) * mm, "construction": true});
            skLineSegment(sketch, "E25.top", {"start": v(3.25, 1.75) * mm, "end": v(-3.25, 1.75) * mm, "construction": true});
            skLineSegment(sketch, "E25.left", {"start": v(3.25, -1.75) * mm, "end": v(3.25, 1.75) * mm, "construction": true});
            skLineSegment(sketch, "E25.right", {"start": v(-3.25, -1.75) * mm, "end": v(-3.25, 1.75) * mm, "construction": true});
            skPoint(sketch, "E25.middle", {"position": v(0, 0) * mm});
            skLineSegment(sketch, "E26.bottom", {"start": v(1.6, -4) * mm, "end": v(-1.6, -4) * mm});
            skLineSegment(sketch, "E26.top", {"start": v(1.6, -2) * mm, "end": v(-1.6, -2) * mm});
            skLineSegment(sketch, "E26.left", {"start": v(1.6, -4) * mm, "end": v(1.6, -2) * mm});
            skLineSegment(sketch, "E26.right", {"start": v(-1.6, -4) * mm, "end": v(-1.6, -2) * mm});
            skPoint(sketch, "E26.middle", {"position": v(0, -3) * mm});
            skLineSegment(sketch, "E27.bottom", {"start": v(2.87, -4) * mm, "end": v(-2.87, -4) * mm, "construction": true});
            skLineSegment(sketch, "E27.top", {"start": v(2.87, 4) * mm, "end": v(-2.87, 4) * mm, "construction": true});
            skLineSegment(sketch, "E27.left", {"start": v(2.87, -4) * mm, "end": v(2.87, 4) * mm, "construction": true});
            skLineSegment(sketch, "E27.right", {"start": v(-2.87, -4) * mm, "end": v(-2.87, 4) * mm, "construction": true});
            skLineSegment(sketch, "E28.bottom", {"start": v(-0.95, 4) * mm, "end": v(-1.6, 4) * mm});
            skLineSegment(sketch, "E28.top", {"start": v(-0.94, 2) * mm, "end": v(-1.6, 2) * mm});
            skLineSegment(sketch, "E28.left", {"start": v(-0.95, 4) * mm, "end": v(-0.94, 2) * mm});
            skLineSegment(sketch, "E28.right", {"start": v(-1.6, 4) * mm, "end": v(-1.6, 2) * mm});
            skPoint(sketch, "E28.middle", {"position": v(-1.27, 3) * mm});
            skLineSegment(sketch, "E29.bottom", {"start": v(1.6, 4) * mm, "end": v(0.95, 4) * mm});
            skLineSegment(sketch, "E29.top", {"start": v(1.6, 2) * mm, "end": v(0.95, 2) * mm});
            skLineSegment(sketch, "E29.left", {"start": v(1.6, 4) * mm, "end": v(1.6, 2) * mm});
            skLineSegment(sketch, "E29.right", {"start": v(0.95, 4) * mm, "end": v(0.95, 2) * mm});
            skPoint(sketch, "E29.middle", {"position": v(1.27, 3) * mm});
            skSolve(sketch);
        }
    });
